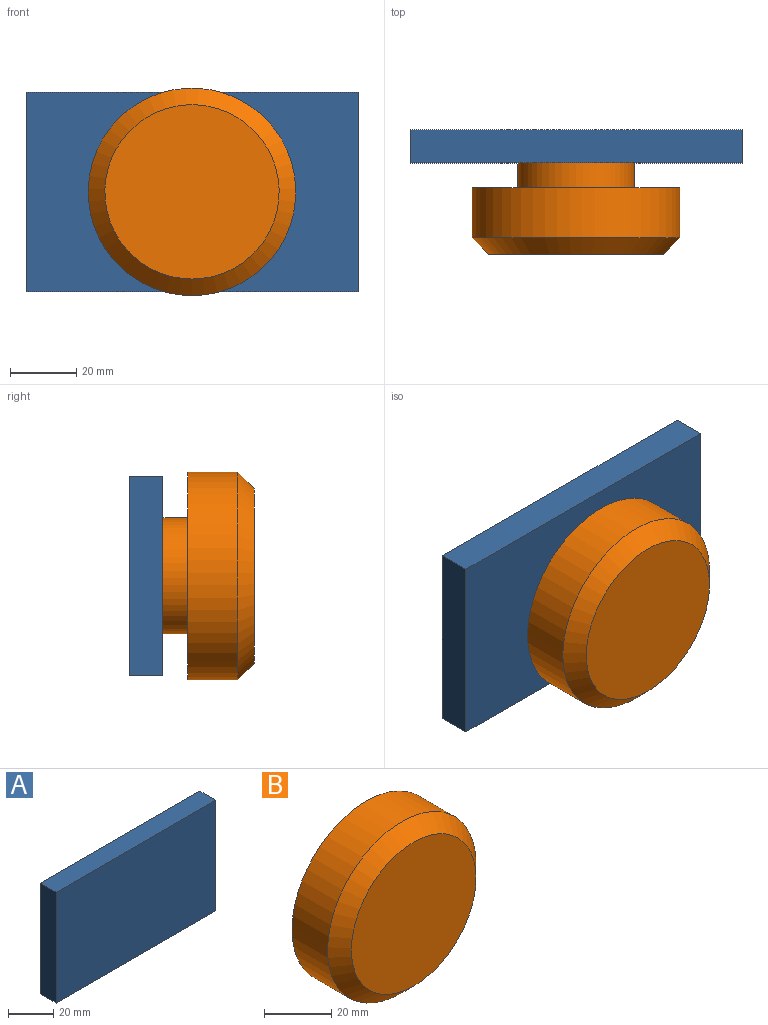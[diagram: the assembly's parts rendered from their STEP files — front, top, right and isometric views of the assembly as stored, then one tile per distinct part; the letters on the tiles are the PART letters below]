
ASSEMBLY  parts=2 mates=2
PART A: 6 faces, bbox 100x10x60 mm
  f0: plane 100x10mm, normal (0,0,1), area 1000mm2, adj f1,f3,f4,f5
  f1: plane 60x10mm, normal (-1,0,0), area 600mm2, adj f0,f2,f4,f5
  f2: plane 100x10mm, normal (0,0,-1), area 1000mm2, adj f1,f3,f4,f5
  f3: plane 60x10mm, normal (1,0,0), area 600mm2, adj f0,f2,f4,f5
  f4: plane 100x60mm, normal (0,-1,0), area 6000mm2, adj f0,f1,f2,f3
  f5: plane 100x60mm, normal (0,1,0), area 6000mm2, adj f0,f1,f2,f3
PART B: 6 faces, bbox 62.5x27.5x62.5 mm
  f0: cylinder r=31.25mm len=62.5mm, axis (0,1,0), area 2945.2mm2, adj f2,f3
  f1: plane 52.5x52.5mm, normal (0,-1,0), area 2164.8mm2, adj f3
  f2: plane 62.5x62.5mm, normal (0,1,0), area 2105.8mm2, adj f0,f4
  f3: cone r=26.25mm half-angle=45deg, axis (0,1,0), area 1277.3mm2, adj f0,f1
  f4: cylinder r=17.5mm len=35mm, axis (0,-1,0), area 824.7mm2, adj f2,f5
  f5: plane 35x35mm, normal (0,1,0), area 962.1mm2, adj f4
PLACE A t=(-8.55,0.43,15.18)mm
PLACE B t=(-8.55,-17.07,15.18)mm
MATE pin_slot B.f4 <-> A.f4  axis (0,-1,0) through (-8.55,-9.57,15.18)mm
MATE fastened B.f4 <-> A.f4  axis (0,-1,0) through (-8.55,-9.57,15.18)mm
